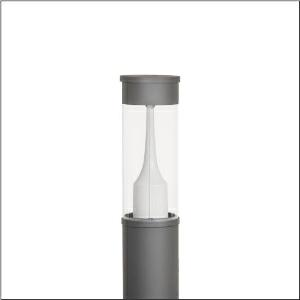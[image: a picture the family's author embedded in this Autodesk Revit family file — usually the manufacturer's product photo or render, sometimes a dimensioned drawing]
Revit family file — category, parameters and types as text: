
# Revit family: city-light_120_iq___pl1_2s_5xa5285rf14h_2286
name_source: partatom
category: Lighting Fixtures
units: mm (PartAtom-declared; Revit-internal decimal feet)

## family parameters
Cut with Voids When Loaded = No
Host = Face
Light Source = No
Part Type = Normal
Room Calculation Point = No
Round Connector Dimension = Use Diameter
Shared = No

## types (1)
- --- (1 x LED, 2970 lm, 18.5 W, 4000K)
    Apparent Load = 19 VA
    CIE Flux Codes = 23 62 94 96 100
    Color Rendering = 70
    Color Temperature = 4000K
    Default Elevation = 1800 mm
    Description = City-Light 120 iQ, bollard luminaire, Module 540 iQ-SR, primary light control with 3 zone facetted reflector, of plastic, silver coated, highly specular, structured, primary optical cover: cover, of PMMA, transparent, partly coated, light distribution: PL1.2s, primary light characteristic: symmetric, LED, High Power LED, rated luminous flux: 2.970lm, luminous efficacy: 161lm/W, light colour: 740, colour temperature: 4000K, control gear: ECG iQ, control: presetting dimming logarithmic, Street-Remote, Auto-Match, Temp-Guard, Lumen-Switch, Night-Set, Smart-Wire, Light-Fading, Desk-Remote (wireless, voltage-free reading and setting of iQ features in the workshop via application-optimized NFC function/RFID function), optimised constant luminous flux control (CLO 2.0), with terminal, 6-pole, max. 2.5mm², mains connection: 230..240V, AC, 50/60Hz, start of lifetime: 19W, end of service life: 20W, reduction: 9W, luminaire housing, cylindrical, of extruded aluminium section, coated, Siteco® metallic grey (DB 702S), length: 1.200mm, diameter: 200mm, Module 540 iQ-SR, traffic white (RAL 9016), equipment: standard, protection rating (complete): IP54, insulation class (complete): insulation class II (safety insulation), certification: CE, ENEC, VDE, packaging unit: 1 piece

Light Distribution: PL1.2s
    Height = 500 mm
    Lamp = 1 x LED
    Lamp Light Flux = 2970 lm
    Lamp Power = 18.5 W
    Lamp count = 1
    Length = 200 mm  [stored 0.656168 ft]
    Luminous efficacy = 161 lm/W
    Manufacturer = Siteco
    ModVariant = No
    Model = 5XA5285RF14H
    Mounting Place = Floor
    Mounting Type = Freestanding
    Number of Poles = 1
    OnlyDefault = Yes
    Power Factor = 1
    Product Name = City-Light 120 iQ | PL1.2s
    Product group = bollard luminaire
    ProductGroupID = 1304
    Protection Class = Protection class II
    Protection Degree = IP 54
    RLX_Detail_Level = 1
    RLX_Emergency_Light_Flux = 0 lm
    RLX_Emergency_Type = 0
    RLX_Emergency_Type_DB = No
    RlxData = <blob elided: 30425 chars, md5=fc852f91>
    Socket = socket
    Standby Power = 0 W
    System Light Flux = 2970 lm
    System Power = 19 W
    Type Comments = factory setting: luminous flux: 100 % | dim-lin: 254 | 385 mA
    Type Image = l_1006922.jpg
    URL = http://relux.com
    VarID = @adj_094725
    Voltage = 0 V
    Weight = 0.00 kg
    Width = 0 mm  [stored 0 ft]

note: [stored X ft] marks values corroborated as IEEE doubles in the binary element streams (Revit-internal decimal feet)

## geometry (parser evidence)
native form markers: Blend x4, Sweep x9
no freeform markers — native parametric forms only
